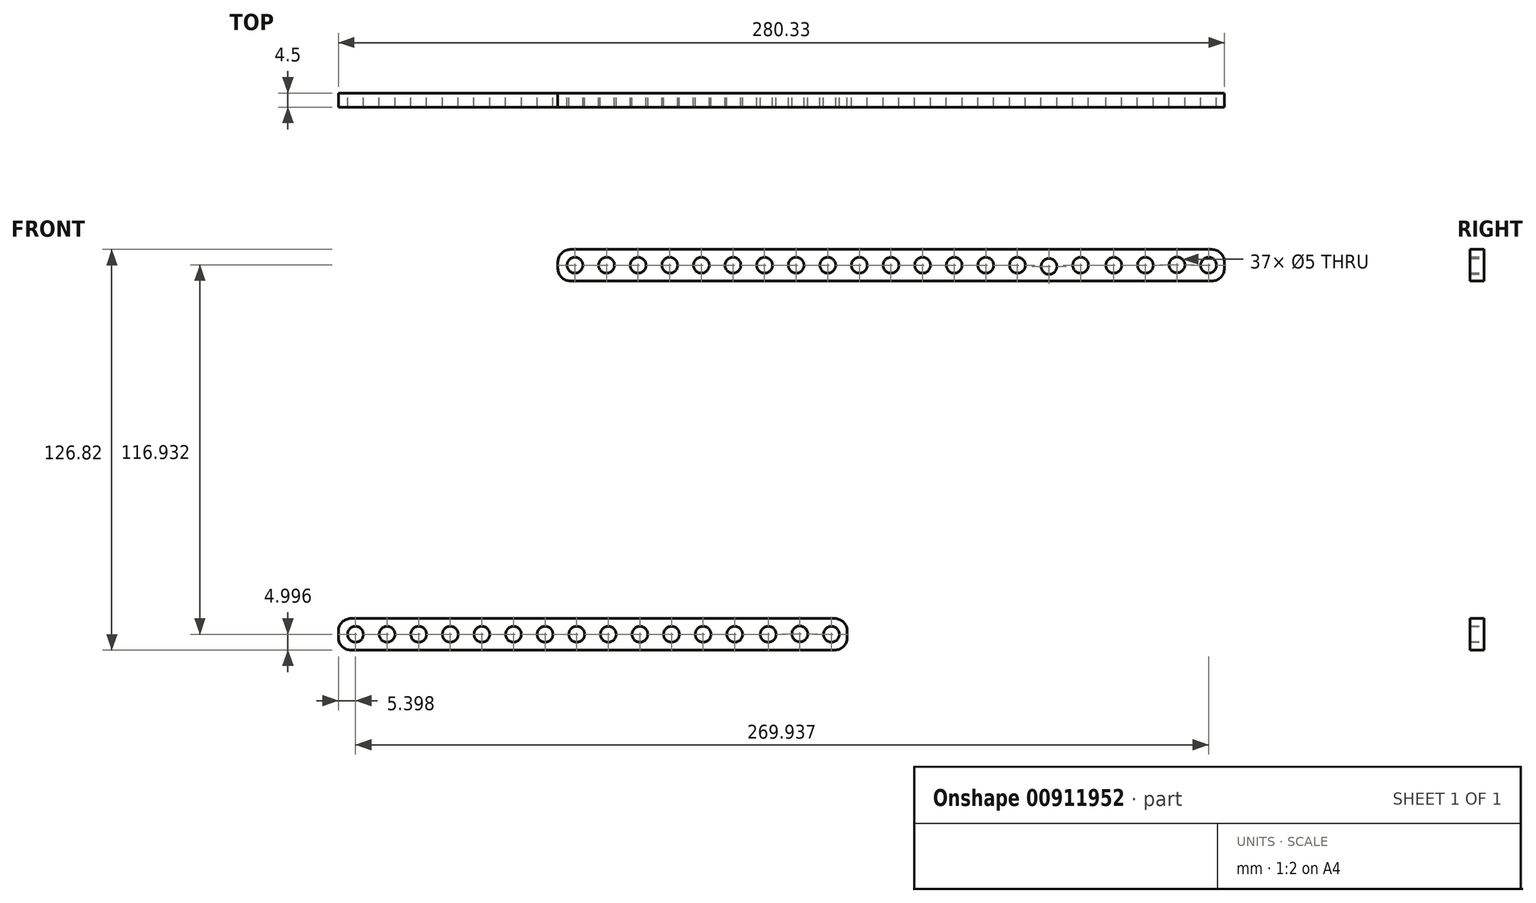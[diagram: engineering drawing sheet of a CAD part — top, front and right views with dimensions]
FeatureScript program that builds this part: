
annotation { "Feature Type Name" : "Feature", "Feature Type Description" : "" }
export const myFeature = defineFeature(function(context is Context, id is Id, definition is map)
    precondition{}
    {
        {
            var Q0;
            Q0=qCreatedBy(makeId("Front.planeOp"),FACE);
            var sketch = newSketch(context, id + "F0", { "sketchPlane" : qUnion([Q0])});
            skLineSegment(sketch, "E0.bottom", {"start": v(-29.45, 22.82) * mm, "end": v(173.44, 22.82) * mm});
            skLineSegment(sketch, "E0.top", {"start": v(-29.45, 12.82) * mm, "end": v(173.44, 12.82) * mm});
            skLineSegment(sketch, "E0.left", {"start": v(-33.45, 18.82) * mm, "end": v(-33.45, 16.82) * mm});
            skLineSegment(sketch, "E0.right", {"start": v(177.44, 18.82) * mm, "end": v(177.44, 16.82) * mm});
            skCircle(sketch, "E1", {"center": v(-28.05, 17.82) * mm, "radius": 2.5 * mm});
            skCircle(sketch, "E2", {"center": v(-18.05, 17.82) * mm, "radius": 2.5 * mm});
            skCircle(sketch, "E3", {"center": v(-8.05, 17.82) * mm, "radius": 2.5 * mm});
            skCircle(sketch, "E4", {"center": v(1.95, 17.82) * mm, "radius": 2.5 * mm});
            skCircle(sketch, "E5", {"center": v(11.95, 17.82) * mm, "radius": 2.5 * mm});
            skCircle(sketch, "E6", {"center": v(21.95, 17.82) * mm, "radius": 2.5 * mm});
            skCircle(sketch, "E7", {"center": v(31.95, 17.82) * mm, "radius": 2.5 * mm});
            skCircle(sketch, "E8", {"center": v(41.95, 17.82) * mm, "radius": 2.5 * mm});
            skCircle(sketch, "E9", {"center": v(51.95, 17.82) * mm, "radius": 2.5 * mm});
            skCircle(sketch, "E10", {"center": v(61.95, 17.82) * mm, "radius": 2.5 * mm});
            skCircle(sketch, "E11", {"center": v(71.95, 17.82) * mm, "radius": 2.5 * mm});
            skCircle(sketch, "E12", {"center": v(81.95, 17.82) * mm, "radius": 2.5 * mm});
            skCircle(sketch, "E13", {"center": v(91.95, 17.82) * mm, "radius": 2.5 * mm});
            skCircle(sketch, "E14", {"center": v(101.95, 17.82) * mm, "radius": 2.5 * mm});
            skPoint(sketch, "E15.visualSharp", {"position": v(-33.45, 22.82) * mm});
            skArc(sketch, "E15.filletArc", {"start": v(-29.45, 22.82) * mm, "mid": v(-32.28, 21.64) * mm, "end": v(-33.45, 18.82) * mm});
            skPoint(sketch, "E16.visualSharp", {"position": v(-33.45, 12.82) * mm});
            skArc(sketch, "E16.filletArc", {"start": v(-33.45, 16.82) * mm, "mid": v(-32.28, 13.99) * mm, "end": v(-29.45, 12.82) * mm});
            skPoint(sketch, "E17.visualSharp", {"position": v(177.44, 22.82) * mm});
            skArc(sketch, "E17.filletArc", {"start": v(177.44, 18.82) * mm, "mid": v(176.27, 21.64) * mm, "end": v(173.44, 22.82) * mm});
            skPoint(sketch, "E18.visualSharp", {"position": v(177.44, 12.82) * mm});
            skArc(sketch, "E18.filletArc", {"start": v(173.44, 12.82) * mm, "mid": v(176.27, 13.99) * mm, "end": v(177.44, 16.82) * mm});
            skCircle(sketch, "E19", {"center": v(111.95, 17.82) * mm, "radius": 2.5 * mm});
            skCircle(sketch, "E20", {"center": v(131.94, 17.82) * mm, "radius": 2.5 * mm});
            skCircle(sketch, "E21", {"center": v(121.95, 17.44) * mm, "radius": 2.5 * mm});
            skCircle(sketch, "E22", {"center": v(142.45, 17.82) * mm, "radius": 2.5 * mm});
            skCircle(sketch, "E23", {"center": v(152.45, 17.82) * mm, "radius": 2.5 * mm});
            skCircle(sketch, "E24", {"center": v(162.45, 17.93) * mm, "radius": 2.5 * mm});
            skCircle(sketch, "E25", {"center": v(172.44, 17.82) * mm, "radius": 2.5 * mm});
            skLineSegment(sketch, "E26.bottom", {"start": v(-98.9, -94) * mm, "end": v(54.1, -94) * mm});
            skLineSegment(sketch, "E26.top", {"start": v(-98.9, -104) * mm, "end": v(54.1, -104) * mm});
            skLineSegment(sketch, "E26.left", {"start": v(-102.9, -98) * mm, "end": v(-102.9, -100) * mm});
            skLineSegment(sketch, "E26.right", {"start": v(58.1, -98) * mm, "end": v(58.1, -100) * mm});
            skCircle(sketch, "E27", {"center": v(-97.5, -99) * mm, "radius": 2.5 * mm});
            skCircle(sketch, "E28", {"center": v(-87.5, -99) * mm, "radius": 2.5 * mm});
            skCircle(sketch, "E29", {"center": v(-77.5, -99) * mm, "radius": 2.5 * mm});
            skCircle(sketch, "E30", {"center": v(-67.5, -99) * mm, "radius": 2.5 * mm});
            skCircle(sketch, "E31", {"center": v(-57.5, -99) * mm, "radius": 2.5 * mm});
            skCircle(sketch, "E32", {"center": v(-47.5, -99) * mm, "radius": 2.5 * mm});
            skCircle(sketch, "E33", {"center": v(-37.5, -99) * mm, "radius": 2.5 * mm});
            skCircle(sketch, "E34", {"center": v(-27.5, -99) * mm, "radius": 2.5 * mm});
            skCircle(sketch, "E35", {"center": v(-17.5, -99) * mm, "radius": 2.5 * mm});
            skCircle(sketch, "E36", {"center": v(-7.5, -99) * mm, "radius": 2.5 * mm});
            skCircle(sketch, "E37", {"center": v(2.5, -99) * mm, "radius": 2.5 * mm});
            skCircle(sketch, "E38", {"center": v(12.5, -99) * mm, "radius": 2.5 * mm});
            skCircle(sketch, "E39", {"center": v(22.5, -99) * mm, "radius": 2.5 * mm});
            skPoint(sketch, "E40.visualSharp", {"position": v(-102.9, -94) * mm});
            skArc(sketch, "E40.filletArc", {"start": v(-98.9, -94) * mm, "mid": v(-101.72, -95.18) * mm, "end": v(-102.9, -98) * mm});
            skPoint(sketch, "E41.visualSharp", {"position": v(-102.9, -104) * mm});
            skArc(sketch, "E41.filletArc", {"start": v(-102.9, -100) * mm, "mid": v(-101.72, -102.83) * mm, "end": v(-98.9, -104) * mm});
            skPoint(sketch, "E42.visualSharp", {"position": v(58.1, -94) * mm});
            skArc(sketch, "E42.filletArc", {"start": v(58.1, -98) * mm, "mid": v(56.94, -95.18) * mm, "end": v(54.1, -94) * mm});
            skPoint(sketch, "E43.visualSharp", {"position": v(58.1, -104) * mm});
            skArc(sketch, "E43.filletArc", {"start": v(54.1, -104) * mm, "mid": v(56.94, -102.83) * mm, "end": v(58.1, -100) * mm});
            skCircle(sketch, "E44", {"center": v(33.1, -99) * mm, "radius": 2.5 * mm});
            skCircle(sketch, "E45", {"center": v(43.1, -98.9) * mm, "radius": 2.5 * mm});
            skCircle(sketch, "E46", {"center": v(53.1, -99) * mm, "radius": 2.5 * mm});
            skPoint(sketch, "E47.center.orphan", {"position": v(62.5, -99) * mm});
            skPoint(sketch, "E48.center.orphan", {"position": v(52.5, -99.38) * mm});
            skPoint(sketch, "E49.center.orphan", {"position": v(42.5, -99) * mm});
            skPoint(sketch, "E50.center.orphan", {"position": v(32.5, -99) * mm});
            skPoint(sketch, "E51.center.orphan", {"position": v(23.1, -99) * mm});
            skSolve(sketch);
        }
        {
            var Q0;
            Q0=makeQuery(id+"F0.imprint","IMPRINT",FACE,{"disambiguationData":[TD([[makeQuery(id+"F0.imprint","IMPRINT",EDGE,{"derivedFrom":sQuery(id+"F0.wireOp",EDGE,"E0.bottom")}),-1.0]])]});
            var Q1;
            Q1=makeQuery(id+"F0.imprint","IMPRINT",FACE,{"disambiguationData":[TD([[makeQuery(id+"F0.imprint","IMPRINT",EDGE,{"derivedFrom":sQuery(id+"F0.wireOp",EDGE,"70d934ce-e17f-45e3-ae2d-8f623205eb24.bottom")}),-1.0]])]});
            extrude(context, id + "F1", {"entities" : qUnion([Q0, Q1]), "depth" : 4.5 * mm, "offsetDistance" : 25 * mm});
        }
        {
            var Q0;
            Q0=makeQuery(id+"F0.imprint","IMPRINT",FACE,{"disambiguationData":[TD([[makeQuery(id+"F0.imprint","IMPRINT",EDGE,{"derivedFrom":sQuery(id+"F0.wireOp",EDGE,"E26.bottom")}),-1.0]])]});
            extrude(context, id + "F2", {"entities" : qUnion([Q0]), "depth" : 4.5 * mm, "offsetDistance" : 25 * mm});
        }
    });
